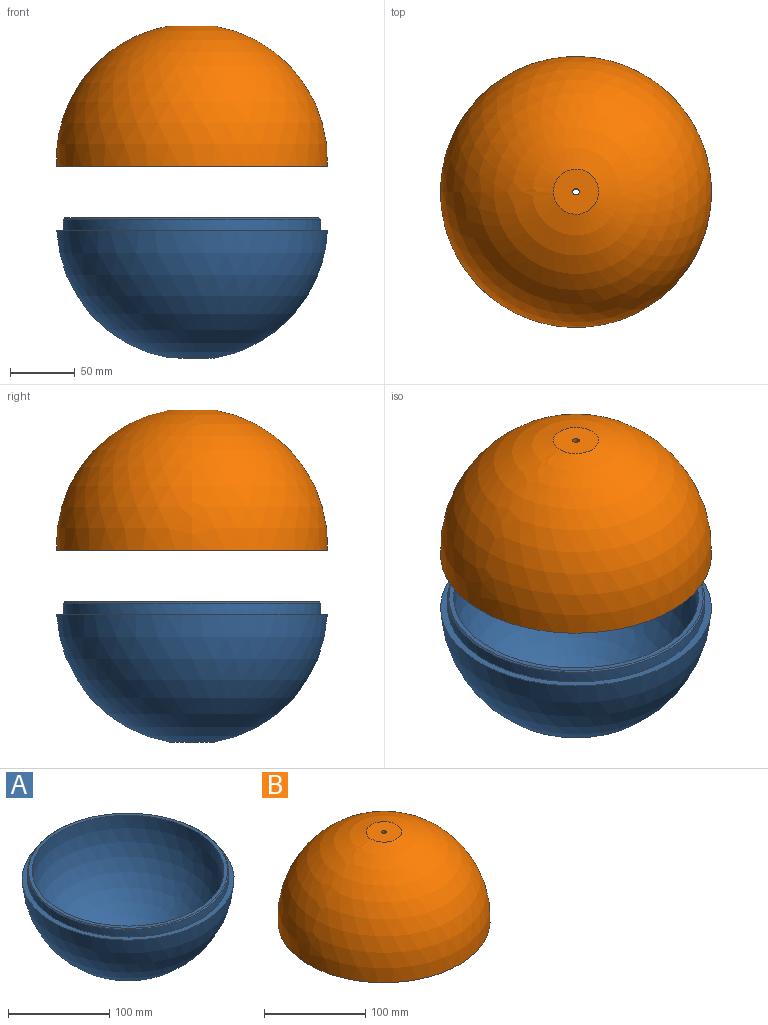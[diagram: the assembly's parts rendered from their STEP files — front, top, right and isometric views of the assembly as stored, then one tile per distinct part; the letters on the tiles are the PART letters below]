
ASSEMBLY  parts=2 mates=1
PART A: 8 faces, bbox 209.8x209.8x108.5 mm
  f0: sphere r=95mm, area 59669.8mm2, adj f5,f7
  f1: cylinder r=99.5mm len=199mm, axis (0,0,1), area 5626.6mm2, adj f2,f6
  f2: plane 209.76x209.76mm, normal (0,0,1), area 3455mm2, adj f1,f3
  f3: sphere r=105mm, area 65004.6mm2, adj f2,f4
  f4: plane 35x35mm, normal (0,0,-1), area 941.6mm2, adj f3,f7
  f5: plane 197x197mm, normal (0,0,1), area 2206.2mm2, adj f0,f6
  f6: cone r=98.5mm half-angle=45deg, axis (0,0,-1), area 879.7mm2, adj f1,f5
  f7: cylinder r=2.55mm len=8.57mm, axis (0,0,-1), area 137.4mm2, adj f0,f4
PART B: 8 faces, bbox 210x210x108.5 mm
  f0: sphere r=95mm, area 53700.8mm2, adj f2,f7
  f1: cylinder r=100.5mm len=201mm, axis (0,0,-1), area 5683.1mm2, adj f2,f6
  f2: plane 201x201mm, normal (0,0,-1), area 3456.5mm2, adj f0,f1
  f3: plane 35x35mm, normal (0,0,1), area 941.6mm2, adj f4,f7
  f4: sphere r=105mm, area 71601.9mm2, adj f3,f5
  f5: plane 209.76x209.76mm, normal (0,0,-1), area 2192mm2, adj f4,f6
  f6: cone r=100.5mm half-angle=45deg, axis (0,0,-1), area 897.5mm2, adj f1,f5
  f7: cylinder r=2.55mm len=8.57mm, axis (0,0,1), area 137.4mm2, adj f0,f3
PLACE A t=(0,0,-50)mm
PLACE B at identity
MATE revolute A.f7 <-> B.f7  axis (0,0,1) through (0,0,-50)mm
